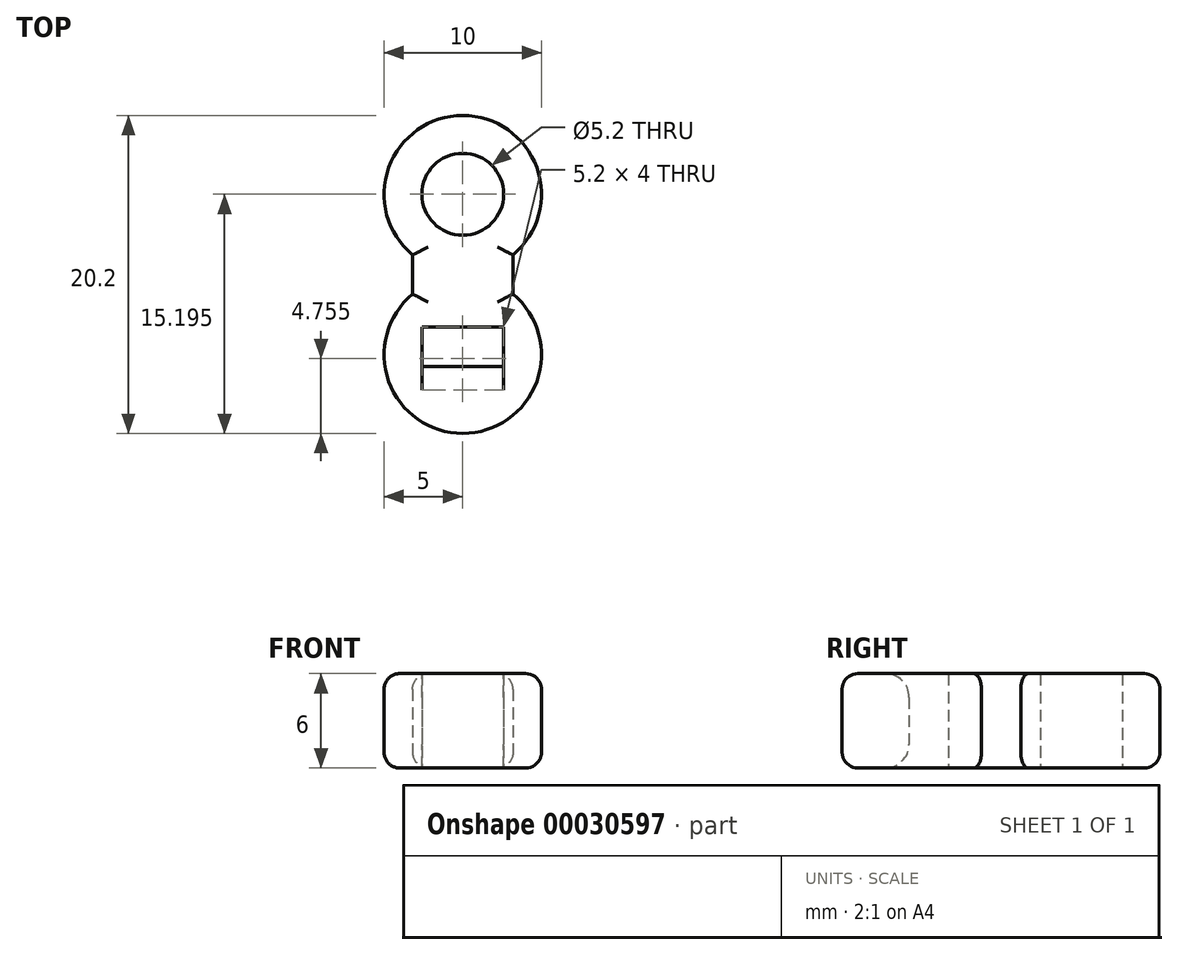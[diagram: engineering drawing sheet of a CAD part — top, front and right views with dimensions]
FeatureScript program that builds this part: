
annotation { "Feature Type Name" : "Feature", "Feature Type Description" : "" }
export const myFeature = defineFeature(function(context is Context, id is Id, definition is map)
    precondition{}
    {
        {
            var Q0;
            Q0=qCreatedBy(makeId("Top.planeOp"),FACE);
            var sketch = newSketch(context, id + "F0", { "sketchPlane" : qUnion([Q0])});
            skCircle(sketch, "E0", {"center": v(0, 5.1) * mm, "radius": 5 * mm});
            skCircle(sketch, "E1", {"center": v(0, -5.1) * mm, "radius": 5 * mm});
            skLineSegment(sketch, "E2", {"start": v(-3.2, 1.25) * mm, "end": v(-3.2, 0) * mm});
            skLineSegment(sketch, "E3", {"start": v(-3.2, 0) * mm, "end": v(-3.2, -1.25) * mm});
            skLineSegment(sketch, "E4", {"start": v(3.2, 1.25) * mm, "end": v(3.2, -1.25) * mm});
            skLineSegment(sketch, "E5", {"start": v(0, 0) * mm, "end": v(-3.2, 0) * mm});
            skLineSegment(sketch, "E6", {"start": v(0, 0) * mm, "end": v(3.2, 0) * mm});
            skCircle(sketch, "E7", {"center": v(0, 5.1) * mm, "radius": 2.6 * mm});
            skLineSegment(sketch, "E8.rect.bottom", {"start": v(-2.6, -3.35) * mm, "end": v(2.6, -3.35) * mm});
            skLineSegment(sketch, "E8.rect.top", {"start": v(-2.6, -5.85) * mm, "end": v(2.6, -5.85) * mm});
            skLineSegment(sketch, "E8.rect.left", {"start": v(-2.6, -3.35) * mm, "end": v(-2.6, -5.85) * mm});
            skLineSegment(sketch, "E8.rect.right", {"start": v(2.6, -3.35) * mm, "end": v(2.6, -5.85) * mm});
            skPoint(sketch, "E8.rect.middle", {"position": v(0, -4.6) * mm});
            skSolve(sketch);
        }
        {
            var Q0;
            Q0 = qSketchRegion(id + "F0", true);
            extrude(context, id + "F1", {"entities" : qUnion([Q0]), "depth" : 6 * mm});
        }
        {
            var Q0;
            Q0=makeQuery(id+"F1.opExtrude","CAP_EDGE",EDGE,{"disambiguationData":[OSD([sQuery(id+"F0.wireOp",EDGE,"E8.rect.top")])],"isStart":false});
            var Q1;
            Q1=makeQuery(id+"F1.opExtrude","CAP_EDGE",EDGE,{"disambiguationData":[OSD([sQuery(id+"F0.wireOp",EDGE,"E8.rect.top")])],"isStart":true});
            fillet(context, id + "F2", {"entities" : qUnion([Q0, Q1]), "radius" : 1.5 * mm, "tangentPropagation" : true, "allowEdgeOverflow" : false});
        }
        {
            var Q0;
            Q0=makeQuery(id+"F1.opExtrude","CAP_EDGE",EDGE,{"disambiguationData":[OSD([sQuery(id+"F0.wireOp",EDGE,"E2"),sQuery(id+"F0.wireOp",EDGE,"E3")])],"isStart":false});
            var Q1;
            Q1=makeQuery(id+"F1.opExtrude","CAP_EDGE",EDGE,{"disambiguationData":[OSD([sQuery(id+"F0.wireOp",EDGE,"E0")])],"isStart":false});
            var Q2;
            Q2=makeQuery(id+"F1.opExtrude","CAP_EDGE",EDGE,{"disambiguationData":[OSD([sQuery(id+"F0.wireOp",EDGE,"E4")])],"isStart":false});
            var Q3;
            Q3=makeQuery(id+"F1.opExtrude","CAP_EDGE",EDGE,{"disambiguationData":[OSD([sQuery(id+"F0.wireOp",EDGE,"E1")])],"isStart":false});
            var Q4;
            Q4=makeQuery(id+"F1.opExtrude","CAP_EDGE",EDGE,{"disambiguationData":[OSD([sQuery(id+"F0.wireOp",EDGE,"E0")])],"isStart":true});
            var Q5;
            Q5=makeQuery(id+"F1.opExtrude","CAP_EDGE",EDGE,{"disambiguationData":[OSD([sQuery(id+"F0.wireOp",EDGE,"E4")])],"isStart":true});
            var Q6;
            Q6=makeQuery(id+"F1.opExtrude","CAP_EDGE",EDGE,{"disambiguationData":[OSD([sQuery(id+"F0.wireOp",EDGE,"E2"),sQuery(id+"F0.wireOp",EDGE,"E3")])],"isStart":true});
            var Q7;
            Q7=makeQuery(id+"F1.opExtrude","CAP_EDGE",EDGE,{"disambiguationData":[OSD([sQuery(id+"F0.wireOp",EDGE,"E1")])],"isStart":true});
            fillet(context, id + "F3", {"entities" : qUnion([Q0, Q1, Q2, Q3, Q4, Q5, Q6, Q7]), "radius" : 1 * mm, "tangentPropagation" : true, "allowEdgeOverflow" : false});
        }
    });
